# Revit family: Haworth_SpceEnabler_Eddy_Table_AP_PRELIMINARY
name_source: partatom
category: Furniture Systems
revit_build: Autodesk Revit 2018 (Build: 20170223_1515(x64)
units: mm (PartAtom-declared; Revit-internal decimal feet)

## family parameters
Always vertical = Yes
Cut with Voids When Loaded = No
OmniClass Number = 23.40.70.14.64.21
OmniClass Title = Systems Furniture
Part Type = Normal
Room Calculation Point = No
Round Connector Dimension = Use Diameter
Shared = No
Work Plane-Based = No

## types (2) — shared parameters
Actual Depth = 520 mm  [stored 1.70604 ft]
Actual Width = 950 mm  [stored 3.1168 ft]
Assembly Code = E2020200
Description = Haworth - Space Enabler - Table - Eddy
Leg Finish = Haworth _ Paint _ Gray Tone
Leg Offset = 100 mm  [stored 0.328084 ft]
Manufacturer = Haworth
Model = SYSEED
Revision Number = 1
Size = Verify Final Dim. w/ Haworth
Table Finish = Haworth _ Polymer _ Snow
Top Thickness = 19 mm  [stored 0.062336 ft]
URL = https://www.haworth.com
URL - Product = https://www.haworth.com
Warranty = http://www.haworth.com

## per-type parameters (varying)
| type | Actual Height | Adjustable | Fixed |
| Adjustable Height | 1020 mm  [stored 3.34646 ft] | Yes | No |
| Fixed Height | 730 mm  [stored 2.39501 ft] | No | Yes |

note: [stored X ft] marks values corroborated as IEEE doubles in the binary element streams (Revit-internal decimal feet)

## geometry (parser evidence)
native form markers: Sweep x3
no freeform markers — native parametric forms only
